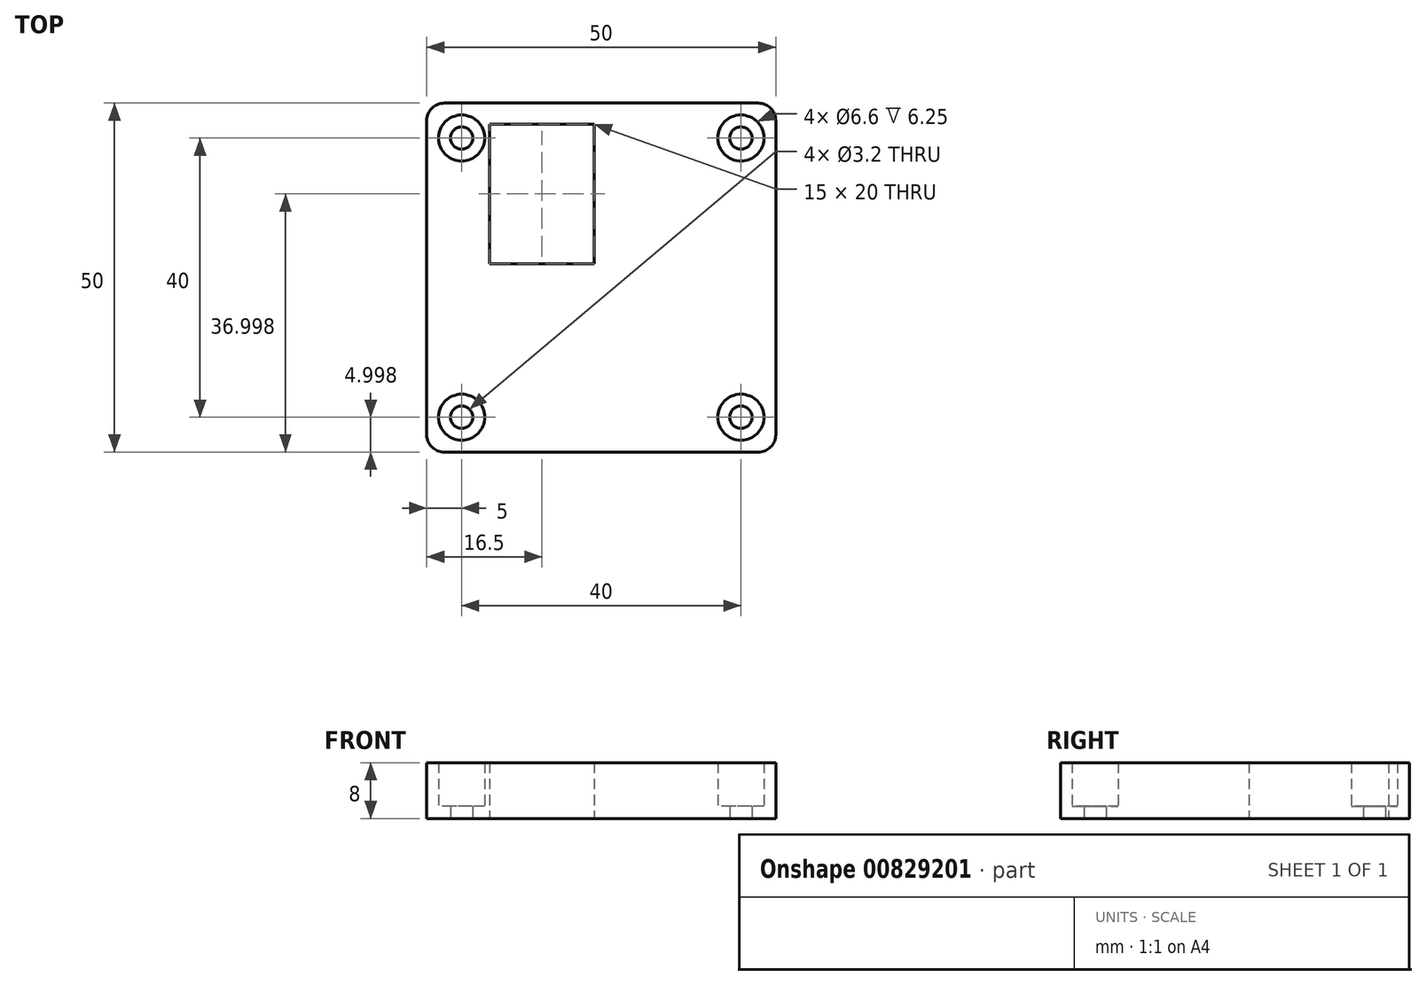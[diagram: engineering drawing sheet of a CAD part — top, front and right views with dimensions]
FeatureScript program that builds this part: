
annotation { "Feature Type Name" : "Feature", "Feature Type Description" : "" }
export const myFeature = defineFeature(function(context is Context, id is Id, definition is map)
    precondition{}
    {
        {
            var Q0;
            Q0=qCreatedBy(makeId("Top.planeOp"),FACE);
            var sketch = newSketch(context, id + "F0", { "sketchPlane" : qUnion([Q0])});
            skLineSegment(sketch, "E0.bottom", {"start": v(-24, 21.65) * mm, "end": v(26, 21.65) * mm});
            skLineSegment(sketch, "E0.top", {"start": v(-24, -28.35) * mm, "end": v(26, -28.35) * mm});
            skLineSegment(sketch, "E0.left", {"start": v(-24, 21.65) * mm, "end": v(-24, -28.35) * mm});
            skLineSegment(sketch, "E0.right", {"start": v(26, 21.65) * mm, "end": v(26, -28.35) * mm});
            skLineSegment(sketch, "E1.bottom", {"start": v(-19, 16.65) * mm, "end": v(21, 16.65) * mm, "construction": true});
            skLineSegment(sketch, "E1.top", {"start": v(-19, -23.35) * mm, "end": v(21, -23.35) * mm, "construction": true});
            skLineSegment(sketch, "E1.left", {"start": v(-19, 16.65) * mm, "end": v(-19, -23.35) * mm, "construction": true});
            skLineSegment(sketch, "E1.right", {"start": v(21, 16.65) * mm, "end": v(21, -23.35) * mm, "construction": true});
            skCircle(sketch, "E2", {"center": v(21, 16.65) * mm, "radius": 3.3 * mm});
            skCircle(sketch, "E3", {"center": v(-19, 16.65) * mm, "radius": 3.3 * mm});
            skCircle(sketch, "E4", {"center": v(-19, -23.35) * mm, "radius": 3.3 * mm});
            skCircle(sketch, "E5", {"center": v(21, -23.35) * mm, "radius": 3.3 * mm});
            skCircle(sketch, "E6", {"center": v(-19, 16.65) * mm, "radius": 1.6 * mm});
            skCircle(sketch, "E7", {"center": v(21, 16.65) * mm, "radius": 1.6 * mm});
            skCircle(sketch, "E8", {"center": v(21, -23.35) * mm, "radius": 1.6 * mm});
            skCircle(sketch, "E9", {"center": v(-19, -23.35) * mm, "radius": 1.6 * mm});
            skLineSegment(sketch, "E10", {"start": v(-24, 0) * mm, "end": v(26, 0) * mm, "construction": true});
            skLineSegment(sketch, "E11.bottom", {"start": v(-15, 18.65) * mm, "end": v(0, 18.65) * mm});
            skLineSegment(sketch, "E11.top", {"start": v(-15, -1.35) * mm, "end": v(0, -1.35) * mm});
            skLineSegment(sketch, "E11.left", {"start": v(-15, 18.65) * mm, "end": v(-15, -1.35) * mm});
            skLineSegment(sketch, "E11.right", {"start": v(0, 18.65) * mm, "end": v(0, -1.35) * mm});
            skSolve(sketch);
        }
        {
            var Q0;
            Q0=makeQuery(id+"F0.imprint","IMPRINT",FACE,{"disambiguationData":[TD([[makeQuery(id+"F0.imprint","IMPRINT",EDGE,{"derivedFrom":sQuery(id+"F0.wireOp",EDGE,"E0.bottom")}),-1.0]])]});
            extrude(context, id + "F1", {"entities" : qUnion([Q0]), "depth" : 8 * mm, "offsetDistance" : 25 * mm});
        }
        {
            var Q0;
            Q0=makeQuery(id+"F0.imprint","IMPRINT",FACE,{"disambiguationData":[TD([[makeQuery(id+"F0.imprint","IMPRINT",EDGE,{"derivedFrom":sQuery(id+"F0.wireOp",EDGE,"E0.bottom")}),-1.0]])]});
            var Q1;
            Q1=makeQuery(id+"F0.imprint","IMPRINT",FACE,{"disambiguationData":[TD([[makeQuery(id+"F0.imprint","IMPRINT",EDGE,{"derivedFrom":sQuery(id+"F0.wireOp",EDGE,"E2")}),1.0]])]});
            var Q2;
            Q2=makeQuery(id+"F0.imprint","IMPRINT",FACE,{"disambiguationData":[TD([[makeQuery(id+"F0.imprint","IMPRINT",EDGE,{"derivedFrom":sQuery(id+"F0.wireOp",EDGE,"E3")}),1.0]])]});
            var Q3;
            Q3=makeQuery(id+"F0.imprint","IMPRINT",FACE,{"disambiguationData":[TD([[makeQuery(id+"F0.imprint","IMPRINT",EDGE,{"derivedFrom":sQuery(id+"F0.wireOp",EDGE,"E4")}),1.0]])]});
            var Q4;
            Q4=makeQuery(id+"F0.imprint","IMPRINT",FACE,{"disambiguationData":[TD([[makeQuery(id+"F0.imprint","IMPRINT",EDGE,{"derivedFrom":sQuery(id+"F0.wireOp",EDGE,"E5")}),1.0]])]});
            extrude(context, id + "F2", {"entities" : qUnion([Q0, Q1, Q2, Q3, Q4]), "operationType" : NewBodyOperationType.ADD, "depth" : 1.75 * mm, "offsetDistance" : 25 * mm});
        }
        {
            var Q0;
            Q0=makeQuery(id+"F1.opExtrude","SWEPT_EDGE",EDGE,{"disambiguationData":[OSD([sQuery(id+"F0.wireOp",EDGE,"E0.bottom"),sQuery(id+"F0.wireOp",EDGE,"E0.left")])]});
            var Q1;
            Q1=makeQuery(id+"F1.opExtrude","SWEPT_EDGE",EDGE,{"disambiguationData":[OSD([sQuery(id+"F0.wireOp",EDGE,"E0.bottom"),sQuery(id+"F0.wireOp",EDGE,"E0.right")])]});
            var Q2;
            Q2=makeQuery(id+"F1.opExtrude","SWEPT_EDGE",EDGE,{"disambiguationData":[OSD([sQuery(id+"F0.wireOp",EDGE,"E0.top"),sQuery(id+"F0.wireOp",EDGE,"E0.right")])]});
            var Q3;
            Q3=makeQuery(id+"F1.opExtrude","SWEPT_EDGE",EDGE,{"disambiguationData":[OSD([sQuery(id+"F0.wireOp",EDGE,"E0.top"),sQuery(id+"F0.wireOp",EDGE,"E0.left")])]});
            fillet(context, id + "F3", {"entities" : qUnion([Q0, Q1, Q2, Q3]), "radius" : 2.5 * mm, "tangentPropagation" : true, "allowEdgeOverflow" : false});
        }
    });
